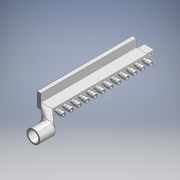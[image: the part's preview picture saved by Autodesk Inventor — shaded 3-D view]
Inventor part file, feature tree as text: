
AUTODESK INVENTOR PART (.ipt)
format: ipt  version: 2018 (Build 220112000, 112)  size: 431,104 bytes
history: native  units: in
note: dims shown in document units (in); Inventor stores cm internally (conversion verified against a paired STEP export)
features: other x10, extrude x5, pattern_linear x2, loft x2, fillet x1, projected_geometry x1, sketch x1
ambient origin geometry x8: Origin, YZ Plane, XZ Plane, XY Plane, X Axis, Y Axis, Z Axis, Center Point
bodies: Body1 (feature_tree)
feature tree (22):
  other  "CrossSection1"
  other  "Silicone Fitting Plane"
  other  "Cap Plane"
  other  "Base Sketch"
  extrude  "Base"  Depth=0.0591in
  extrude  "Extrusion21"  Depth=0.0591in
  other  "Silicone Fitting"
  extrude  "Airflow Cut"  Depth=0.0591in
  extrude  "Coupling"  Depth=0.0197in
  pattern_linear  "Airflow Cut Repetition"  Spacing1=0.5906in  [1 undecoded]
  pattern_linear  "Rectangular Pattern7"  Spacing1=-0.2067in  [1 undecoded]
  other  "Mouthpiece Adapter Plane"
  other  "Mouthpiece Adapter Loft To"
  loft  "Mouthpiece Adapter Outer"
  loft  "Moutpiece Adapter Inner"
  extrude  "Mouthpiece"  Depth=0.1181in TaperAngle=0.0deg
  fillet  "Fillet1"  [1 undecoded]
  other  "Silicone Fitting Sketch"
  other  "Airflow Cut Sketch"
  projected_geometry  "Projected Loop7"
  other  "Coupling Sketch"
  sketch  "Sketch22"  dims[d87=0.0197in d88=0.0787in d89=-1.0625in d90=0.7874in d1=0.0591in d2=0.0591in d3=0.0591in d4=0.0197in d5=0.5906in d6=-0.2067in d8=0.0in d111=90.0deg d112=0.1181in d9=0.0in d12=-4.9606in d13=0.5906in d14=0.3214in d15=0.0in d122=0.7874in d124=0.1607in d125=1.1811in d128=0.0in d129=90.0deg d130=0.0in d131=90.0deg d132=0.0in d133=90.0deg d134=0.0in d135=90.0deg d136=0.7874in d137=0.0in d138=0.5512in d139=0.689in d140=0.7874in d141=0.0591in d142=0.0295in d143=0.0295in d144=0.0295in d145=0.0295in d146=0.0295in d147=0.0295in d148=0.0591in d155=5.1181in d157=0.4134in d158=4.7244in d160=0.4134in d161=4.9606in d162=0.1969in d163=0.7347in d164=0.0in]
note: 3 required parameter values undecoded (feature->parameter linkage not recoverable at this tier; creation-order binding heuristic only, values carry confidence <= 0.55)
